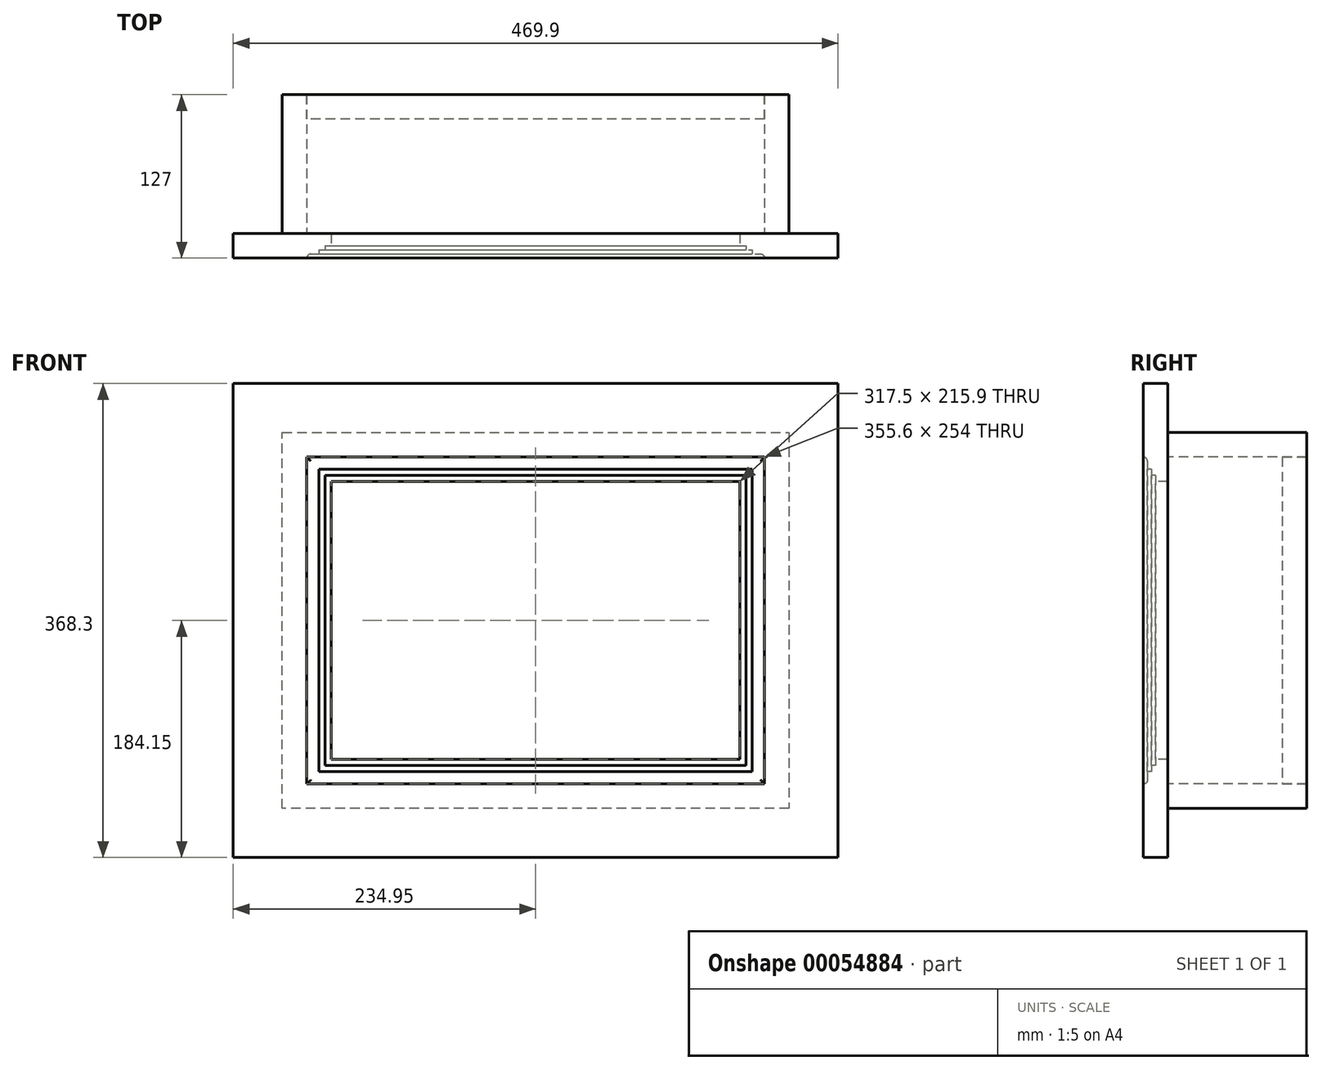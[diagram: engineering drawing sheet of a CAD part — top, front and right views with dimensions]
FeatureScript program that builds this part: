
annotation { "Feature Type Name" : "Feature", "Feature Type Description" : "" }
export const myFeature = defineFeature(function(context is Context, id is Id, definition is map)
    precondition{}
    {
        {
            var Q0;
            Q0=qCreatedBy(makeId("Front.planeOp"),FACE);
            var sketch = newSketch(context, id + "F0", { "sketchPlane" : qUnion([Q0])});
            skLineSegment(sketch, "E0.rect.bottom", {"start": v(177.8, 127) * mm, "end": v(-177.8, 127) * mm});
            skLineSegment(sketch, "E0.rect.top", {"start": v(177.8, -127) * mm, "end": v(-177.8, -127) * mm});
            skLineSegment(sketch, "E0.rect.left", {"start": v(177.8, 127) * mm, "end": v(177.8, -127) * mm});
            skLineSegment(sketch, "E0.rect.right", {"start": v(-177.8, 127) * mm, "end": v(-177.8, -127) * mm});
            skPoint(sketch, "E0.rect.middle", {"position": v(0, 0) * mm});
            skSolve(sketch);
        }
        {
            var Q0;
            Q0=makeQuery(id+"F0.imprint","IMPRINT",FACE,{"disambiguationData":[TD([[makeQuery(id+"F0.imprint","IMPRINT",EDGE,{"derivedFrom":sQuery(id+"F0.wireOp",EDGE,"E0.rect.bottom")}),1.0]])]});
            extrude(context, id + "F1", {"entities" : qUnion([Q0]), "depth" : 19.05 * mm});
        }
        {
            var Q0;
            Q0=qCreatedBy(makeId("Right.planeOp"),FACE);
            var sketch = newSketch(context, id + "F2", { "sketchPlane" : qUnion([Q0])});
            skLineSegment(sketch, "E1.bottom", {"start": v(0, 127) * mm, "end": v(-107.95, 127) * mm});
            skLineSegment(sketch, "E1.top", {"start": v(0, 146.05) * mm, "end": v(-107.95, 146.05) * mm});
            skLineSegment(sketch, "E1.left", {"start": v(0, 146.05) * mm, "end": v(0, 127) * mm});
            skLineSegment(sketch, "E1.right", {"start": v(-107.95, 146.05) * mm, "end": v(-107.95, 127) * mm});
            skSolve(sketch);
        }
        {
            var Q0;
            Q0=makeQuery(id+"F2.imprint","IMPRINT",FACE,{"disambiguationData":[TD([[makeQuery(id+"F2.imprint","IMPRINT",EDGE,{"derivedFrom":sQuery(id+"F2.wireOp",EDGE,"E1.bottom")}),-1.0]])]});
            var Q1;
            Q1=sQuery(id+"F0.wireOp",EDGE,"E0.rect.bottom");
            var Q2;
            Q2=sQuery(id+"F0.wireOp",EDGE,"E0.rect.right");
            var Q3;
            Q3=sQuery(id+"F0.wireOp",EDGE,"E0.rect.top");
            var Q4;
            Q4=sQuery(id+"F0.wireOp",EDGE,"E0.rect.left");
            sweep(context, id + "F3", {"profiles" : qUnion([Q0]), "path" : qUnion([Q1, Q2, Q3, Q4])});
        }
        {
            var Q0;
            Q0=qCreatedBy(makeId("Right.planeOp"),FACE);
            var sketch = newSketch(context, id + "F4", { "sketchPlane" : qUnion([Q0])});
            skLineSegment(sketch, "E2.bottom", {"start": v(-107.95, 184.15) * mm, "end": v(-127, 184.15) * mm});
            skLineSegment(sketch, "E2.left", {"start": v(-107.95, 184.15) * mm, "end": v(-107.95, 127) * mm});
            skLineSegment(sketch, "E2.right", {"start": v(-127, 184.15) * mm, "end": v(-127, 127) * mm});
            skLineSegment(sketch, "E3.0", {"start": v(-107.95, 107.95) * mm, "end": v(-117.48, 107.95) * mm});
            skLineSegment(sketch, "E4", {"start": v(-107.95, 127) * mm, "end": v(-107.95, 107.95) * mm});
            skLineSegment(sketch, "E5.0", {"start": v(-123.83, 123.83) * mm, "end": v(-123.83, 117.47) * mm});
            skPoint(sketch, "E6.visualSharp", {"position": v(-123.83, 127) * mm});
            skArc(sketch, "E6.filletArc", {"start": v(-123.83, 123.83) * mm, "mid": v(-124.75, 126.07) * mm, "end": v(-127, 127) * mm});
            skLineSegment(sketch, "E7", {"start": v(-120.65, 117.47) * mm, "end": v(-123.83, 117.47) * mm});
            skLineSegment(sketch, "E8.0", {"start": v(-120.65, 117.47) * mm, "end": v(-120.65, 112.71) * mm});
            skLineSegment(sketch, "E9.filletArc", {"start": v(-123.83, 127) * mm, "end": v(-123.83, 127) * mm});
            skLineSegment(sketch, "E10", {"start": v(-120.65, 112.71) * mm, "end": v(-117.48, 112.71) * mm});
            skLineSegment(sketch, "E11", {"start": v(-117.48, 112.71) * mm, "end": v(-117.48, 107.95) * mm});
            skSolve(sketch);
        }
        {
            var Q0;
            Q0=makeQuery(id+"F4.imprint","IMPRINT",FACE,{"disambiguationData":[TD([[makeQuery(id+"F4.imprint","IMPRINT",EDGE,{"derivedFrom":sQuery(id+"F4.wireOp",EDGE,"E2.bottom")}),1.0]])]});
            var Q1;
            Q1=sQuery(id+"F0.wireOp",EDGE,"E0.rect.bottom");
            var Q2;
            Q2=sQuery(id+"F0.wireOp",EDGE,"E0.rect.right");
            var Q3;
            Q3=sQuery(id+"F0.wireOp",EDGE,"E0.rect.top");
            var Q4;
            Q4=sQuery(id+"F0.wireOp",EDGE,"E0.rect.left");
            sweep(context, id + "F5", {"profiles" : qUnion([Q0]), "path" : qUnion([Q1, Q2, Q3, Q4])});
        }
    });
